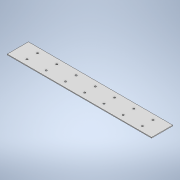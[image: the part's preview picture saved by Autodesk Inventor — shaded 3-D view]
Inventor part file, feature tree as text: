
AUTODESK INVENTOR PART (.ipt)
format: ipt  version: 2022 (Build 260153000, 153)  size: 126,464 bytes
history: native  units: mm
features: sheet_metal_op x1, sketch x1, other x1
ambient origin geometry x8: Origin, YZ Plane, XZ Plane, XY Plane, X Axis, Y Axis, Z Axis, Center Point
bodies: Solid1 (feature_tree)
feature tree (3):
  sheet_metal_op  "Face1"
  sketch  "Sketch1"  dims[d0=44.0mm d1=300.0mm d2=3.5mm d3=11.0mm d4=3.5mm d5=30.0mm d6=30.0mm d7=11.0mm d8=70.0mm d10=40.0mm d11=10.0mm d13=10.0mm d15=1.5mm]
  other  "Plate1"
